# Revit family: Kessel 8743025 en
name_source: partatom
category: Plumbing Fixtures
revit_build: Autodesk Revit Architecture 2014 (Build: 20130308_1515(x64)
units: mm (PartAtom-declared; Revit-internal decimal feet)

## types (1)
- Kessel 8743025 en
    <1.010.00.2> Number of the part of the guideline = 4
    <1.010.00.3> Issue date (month) of the guideline = 201410
    <1.010.00.4> Manufacturer name = Kessel
    <1.010.00.5> Revision date of the file = 20190228
    <1.800.00.3> BS number = 00402200000500200200100100000200100100200000000012???
    <1.800.00.4> Comment field = Aqualift S XL Duo pumping station, GTF 4000-S1, level probe
    <1.810.00.3> Manufacturer’s reference number = 8743025
    <1.810.00.4> DATANORM number = 8743025
    <1.810.00.6> GTIN number = 4026092075791
    <1.960/3L.00.8> Link (URL) = http://www.kessel.de
    <4.100.00.4> Area of application = drainage
    <4.110.00.4> Model series = Aqualift S XL pumping station
    <4.200.00.3> Design type = submersible pump
    <4.250.00.3> Shaft position = vertical
    <4.260.00.3> Construction = dry-rotor pump
    <4.300.00.3> Hydraulic = single-level
    <4.350.00.3> Intake feature = normal-priming
    <4.400.00.3> Actuator = e-motor for three-phase current
    <4.450.00.3> Type of speed adjustment = none
    <4.460.00.3> E-motor startup mode = direct
    <4.500.00.3> Material specifications pump housing = Cast iron
    <4.700.00.10> Star / delta starting circuit with three-phase connection or three-phase current = yes
    <4.700.00.11> Rated frequency [Hz] = 50
    <4.700.00.12> Degree of protection = IP 68
    <4.700.00.13> Heat class = H
    <4.700.00.15> Maximum temperature of pumped medium [°C] = 40
    <4.700.00.16> Minimum temperature of pumped medium [°C] = 0
    <4.700.00.21> Maximum working pressure Pmax PN [hPa] = 1800
    <4.700.00.22> Maximum shaft output (P2) per pump/drive [W] = 3.4
    <4.700.00.23> Nominal speed n [1/min] = 2900
    <4.700.00.24> Maximum speed n [1/min] = 2900
    <4.700.00.25> minimum speed at int. speed adjustment [1/min] = 0
    <4.700.00.26> maximum power consumption per pump / drive [A] = 6.6
    <4.700.00.27> inrush current [A] = 39.6
    <4.700.00.28> Motor-pump shaft = continuous
    <4.700.00.29> shaft seal = Mechanical seal
    <4.700.00.30> Total number of pumps / drives = 2
    <4.700.00.31> Number of operating pumps / drives = 1
    <4.700.00.32> Net mass [kg] = 130
    <4.700.00.33> electrical rating (P1) [W] = 4
    <4.700.00.34> maximum flow [m3/h] = 53
    <4.700.00.37> maximum delivery height [m] = 18
    <4.700.00.44> upper tolerance of the operating voltage (+) [%] = 10
    <4.700.00.45> lower tolerance of the operating voltage (-) [%] = 10
    <4.700.00.46> vertical installation = yes
    <4.700.00.47> outdoor installation = yes
    <4.700.00.48> ATEX = no
    <4.700.00.49> protection class = protection class I
    <4.700.00.4> Product name = Aqualift S XL Duo pumping station, GTF 4000-S1, level probe
    <4.700.00.50> motor protection = internal
    <4.700.00.6> Nominal connection size on pressure side = 50
    <4.700.00.7> Nominal connection size on suction side = 150
    <4.700.00.8> Electrical connection [V] = 400
    <4.700.00.9> Voltage = 3/N/PE 400V
    <4.710.01.10> Type of wastewater disposal plant = Double unit (duo)
    <4.710.01.11> Installation site of the plant = in the shaft
    <4.710.01.12> Installation type of the system = wet
    <4.710.01.13> Mass pump (net) [kg] = 45
    <4.710.01.14> Mass overall system (net) [kg] = 231
    <4.710.01.18> Backflow preventer available = yes
    <4.710.01.19> Type of level control = Conductance probes
    <4.710.01.20> ATEX for switching device = no
    <4.710.01.21> Function switching device = with alarm message
    <4.710.01.22> Variant of the warning device = acoustic signal tone
    <4.710.01.23> Self-diagnosis system for switching device (SDS) = yes
    <4.710.01.24> Logbook function for warning device = yes
    <4.710.01.25> Interface for switching device available = Radio interface (GSM)
    <4.710.01.26> Connection for switching device to GLT, GA = optional
    <4.710.01.27> Display for switching device = yes
    <4.710.01.28> Battery operation of the warning device possible = yes
    <4.710.01.4> Deliverable volume between on and off volume of the collection container [l] = 340
    <4.710.01.5> Cutting device available = no
    <4.710.01.6> free ball passage [mm] = 50
    <4.710.01.7> operating mode = S1
    <4.710.01.9> Type of wastewater plant = Wastewater lifting plant for sewage-free wastewater (EN 12050-2)
    <4.710.02.10> Mass pump (net) [kg] = 45
    <4.710.02.3> free ball passage [mm] = 50
    <4.710.02.4> Attached pump control = yes
    <4.710.02.5> cutter = no
    <4.710.02.6> operating mode = S1
    <4.710.02.8> Application of the wastewater pump = Wastewater lifting plant for sewage-free wastewater (EN 12050-2)
    <4.710.02.9> Location of the pump = in the shaft
    <4.710.03.3> Type of measurements = Dimensions
    <4.710.03.4> length [mm] = 1370
    <4.710.03.5> width [mm] = 1240
    <4.710.03.6> height [mm] = 1416
    <4.710.03.7> Mass (net) [kg] = 231
    CONNECTOR0_DIAMETER_dX_0r = 0 mm  [stored 0 ft]
    CONNECTOR0_dX_00 = 684 mm
    CONNECTOR0_dX_01 = 559 mm
    CONNECTOR0_ref_dX = 559 mm
    CONNECTOR0_ref_dZ = 1134 mm
    CONNECTOR1_DIAMETER_dX_0r = 0 mm  [stored 0 ft]
    CONNECTOR1_dX_00 = 687 mm
    CONNECTOR1_dX_01 = 697 mm
    CONNECTOR1_ref_dX = 687 mm
    CONNECTOR1_ref_dZ = 1134 mm
    Manufacturer = Kessel
    Model = 8743025
    URL = www.kessel.com

note: [stored X ft] marks values corroborated as IEEE doubles in the binary element streams (Revit-internal decimal feet)
